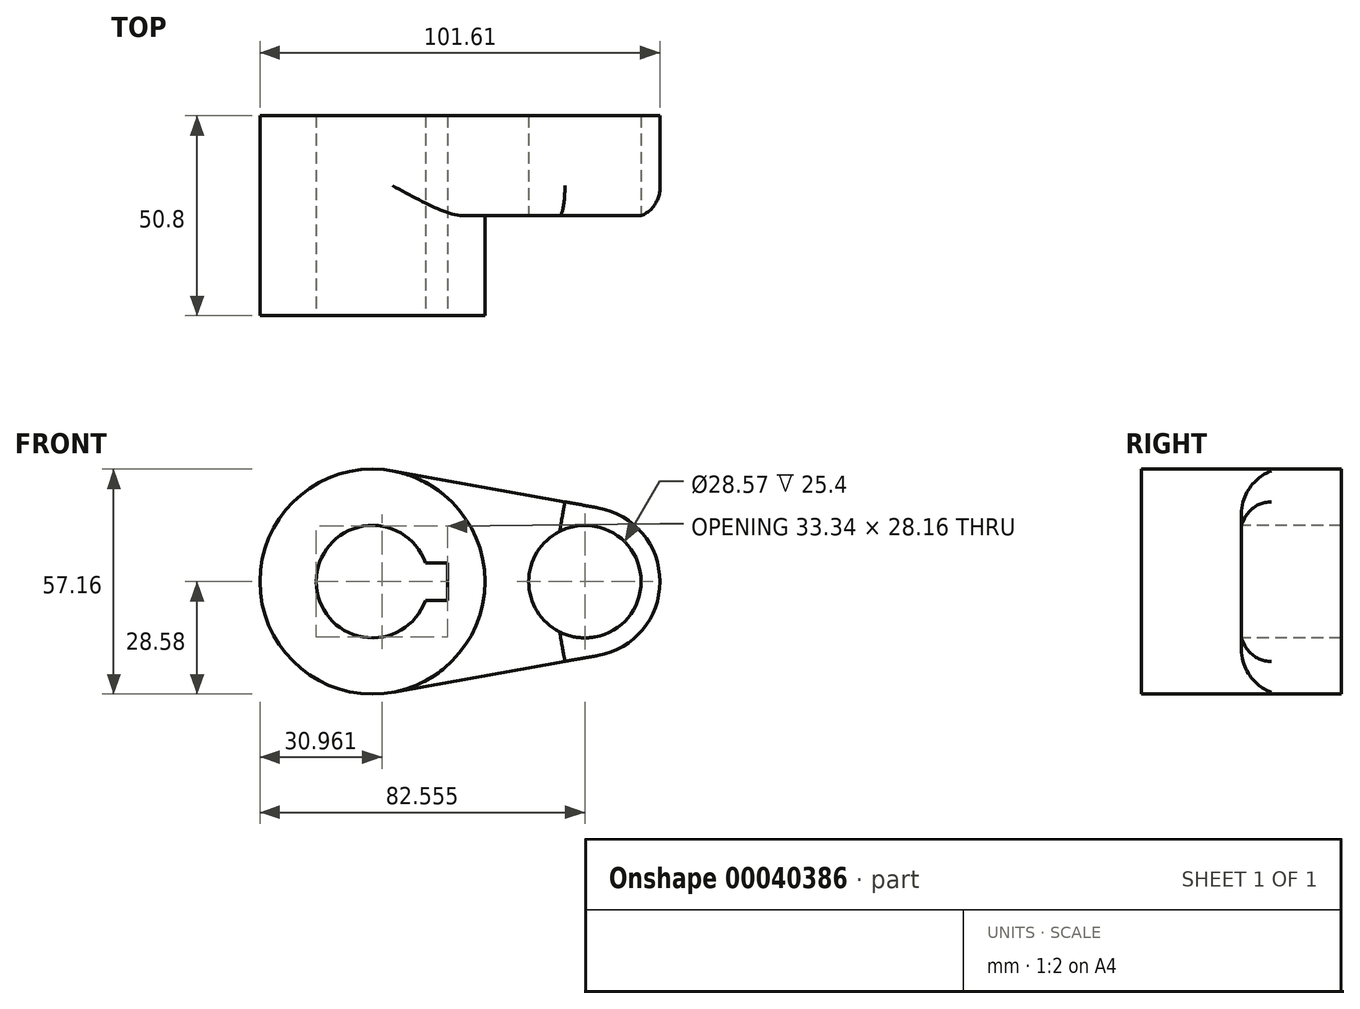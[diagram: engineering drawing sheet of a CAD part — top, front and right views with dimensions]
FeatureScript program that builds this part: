
annotation { "Feature Type Name" : "Feature", "Feature Type Description" : "" }
export const myFeature = defineFeature(function(context is Context, id is Id, definition is map)
    precondition{}
    {
        {
            var Q0;
            Q0=qCreatedBy(makeId("Front.planeOp"),FACE);
            var sketch = newSketch(context, id + "F0", { "sketchPlane" : qUnion([Q0])});
            skCircle(sketch, "E0", {"center": v(0, 0) * mm, "radius": 28.58 * mm});
            skCircle(sketch, "E1", {"center": v(53.98, 0) * mm, "radius": 19.05 * mm});
            skLineSegment(sketch, "E2", {"start": v(5.04, 28.13) * mm, "end": v(57.34, 18.75) * mm});
            skLineSegment(sketch, "E3", {"start": v(5.04, -28.13) * mm, "end": v(57.34, -18.75) * mm});
            skCircle(sketch, "E4", {"center": v(0, 0) * mm, "radius": 14.29 * mm});
            skCircle(sketch, "E5", {"center": v(53.98, 0) * mm, "radius": 14.29 * mm});
            skLineSegment(sketch, "E6.rect.bottom", {"start": v(19.05, -4.76) * mm, "end": v(-19.05, -4.76) * mm});
            skLineSegment(sketch, "E6.rect.top", {"start": v(19.05, 4.76) * mm, "end": v(-19.05, 4.76) * mm});
            skLineSegment(sketch, "E6.rect.left", {"start": v(19.05, -4.76) * mm, "end": v(19.05, 4.76) * mm});
            skLineSegment(sketch, "E6.rect.right", {"start": v(-19.05, -4.76) * mm, "end": v(-19.05, 4.76) * mm});
            skSolve(sketch);
        }
        {
            var Q0;
            {var subQ5=sQuery(id+"F0.wireOp",EDGE,"E6.rect.left");Q0=makeQuery(id+"F0.imprint","IMPRINT",FACE,{"disambiguationData":[TD([[makeQuery(id+"F0.imprint","IMPRINT",EDGE,{"derivedFrom":subQ5}),-1.0]])]});}
            var Q1;
            {var subQ1=sQuery(id+"F0.wireOp",EDGE,"E2");Q1=makeQuery(id+"F0.imprint","IMPRINT",FACE,{"disambiguationData":[TD([[makeQuery(id+"F0.imprint","IMPRINT",EDGE,{"derivedFrom":subQ1}),-1.0]])]});}
            var Q2;
            Q2=makeQuery(id+"F0.imprint","IMPRINT",FACE,{"disambiguationData":[TD([[makeQuery(id+"F0.imprint","IMPRINT",EDGE,{"derivedFrom":sQuery(id+"F0.wireOp",EDGE,"E5")}),-1.0]])]});
            var Q3;
            {var subQ0=sQuery(id+"F0.wireOp",EDGE,"E6.rect.right");Q3=makeQuery(id+"F0.imprint","IMPRINT",FACE,{"disambiguationData":[TD([[makeQuery(id+"F0.imprint","IMPRINT",EDGE,{"derivedFrom":subQ0}),-1.0]])]});}
            extrude(context, id + "F1", {"entities" : qUnion([Q0, Q1, Q2, Q3]), "oppositeDirection" : true, "depth" : 25.4 * mm});
        }
        {
            var Q0;
            {var subQ5=sQuery(id+"F0.wireOp",EDGE,"E6.rect.left");Q0=makeQuery(id+"F0.imprint","IMPRINT",FACE,{"disambiguationData":[TD([[makeQuery(id+"F0.imprint","IMPRINT",EDGE,{"derivedFrom":subQ5}),-1.0]])]});}
            var Q1;
            {var subQ0=sQuery(id+"F0.wireOp",EDGE,"E6.rect.right");Q1=makeQuery(id+"F0.imprint","IMPRINT",FACE,{"disambiguationData":[TD([[makeQuery(id+"F0.imprint","IMPRINT",EDGE,{"derivedFrom":subQ0}),-1.0]])]});}
            extrude(context, id + "F2", {"entities" : qUnion([Q0, Q1]), "operationType" : NewBodyOperationType.ADD, "depth" : 25.4 * mm});
        }
        {
            var Q0;
            Q0=makeQuery(id+"F1.opExtrude","CAP_EDGE",EDGE,{"disambiguationData":[OSD([sQuery(id+"F0.wireOp",EDGE,"E1")])],"isStart":true});
            fillet(context, id + "F3", {"entities" : qUnion([Q0]), "radius" : 7.62 * mm, "tangentPropagation" : true, "allowEdgeOverflow" : false});
        }
    });
